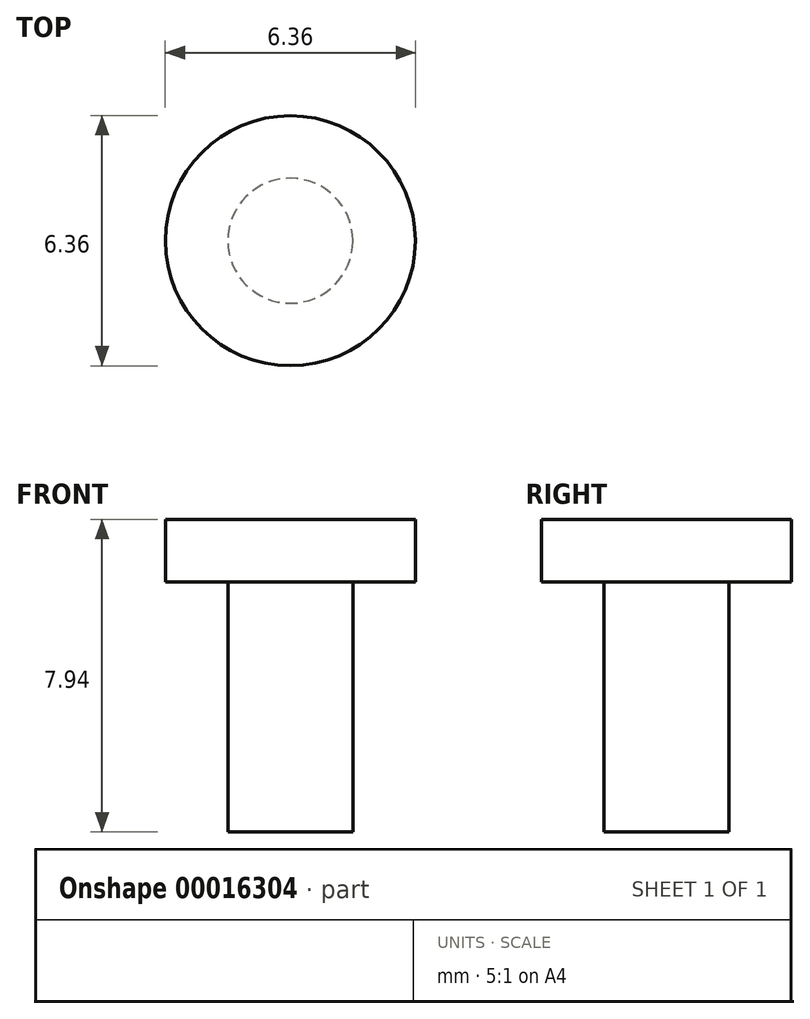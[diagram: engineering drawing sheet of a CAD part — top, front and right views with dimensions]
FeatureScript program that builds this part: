
annotation { "Feature Type Name" : "Feature", "Feature Type Description" : "" }
export const myFeature = defineFeature(function(context is Context, id is Id, definition is map)
    precondition{}
    {
        {
            var Q0;
            Q0=qCreatedBy(makeId("Top.planeOp"),FACE);
            var sketch = newSketch(context, id + "F0", { "sketchPlane" : qUnion([Q0])});
            skCircle(sketch, "E0", {"center": v(0, 0) * mm, "radius": 3.18 * mm});
            skSolve(sketch);
        }
        {
            var Q0;
            Q0 = qSketchRegion(id + "F0", true);
            extrude(context, id + "F1", {"entities" : qUnion([Q0]), "depth" : 1.59 * mm});
        }
        {
            var Q0;
            Q0=makeQuery(id+"F1.opExtrude","CAP_FACE",FACE,{"disambiguationData":[OSD([sQuery(id+"F0.wireOp",EDGE,"E0")])],"isStart":true});
            var sketch = newSketch(context, id + "F2", { "sketchPlane" : qUnion([Q0])});
            skCircle(sketch, "E1", {"center": v(0, 0) * mm, "radius": 1.59 * mm});
            skSolve(sketch);
        }
        {
            var Q0;
            Q0 = qSketchRegion(id + "F2", true);
            extrude(context, id + "F3", {"entities" : qUnion([Q0]), "operationType" : NewBodyOperationType.ADD, "depth" : 6.35 * mm});
        }
    });
